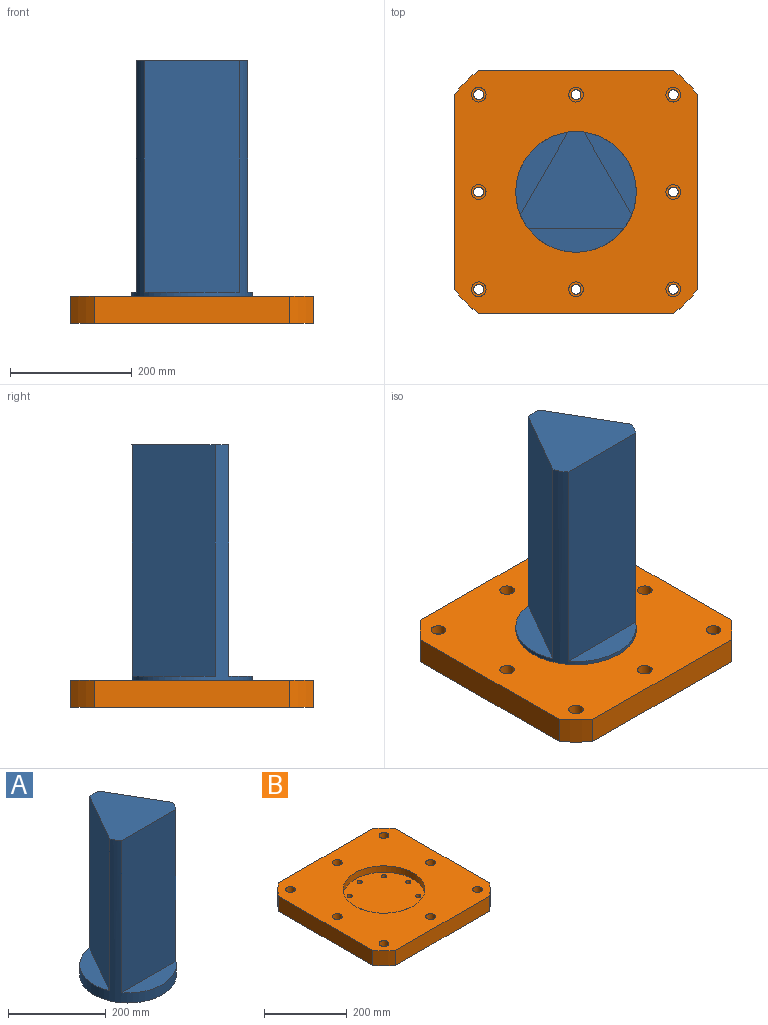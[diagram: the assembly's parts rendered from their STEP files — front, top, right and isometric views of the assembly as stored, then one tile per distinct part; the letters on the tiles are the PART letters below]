
ASSEMBLY  parts=2 mates=2
PART A: 27 faces, bbox 198.1x198.1x406.4 mm
  f0: plane 381x157.15mm, normal (0,-1,0), area 59872.9mm2, adj f3,f4,f5
  f1: plane 381x136.09mm, normal (0.87,0.5,0), area 59872.9mm2, adj f3,f4,f7
  f2: plane 381x136.09mm, normal (-0.87,0.5,0), area 59872.9mm2, adj f3,f4,f6
  f3: cylinder r=99.06mm len=406.4mm, axis (0,0,-1), area 45512.4mm2, adj f0,f1,f2,f4,f5,f6,f7,f8
  f4: plane 183.06x159.39mm, normal (0,0,1), area 18081.2mm2, adj f0,f1,f2,f3
  f5: plane 157.15x38.74mm, normal (0,0,1), area 4249mm2, adj f0,f3
  f6: plane 136.09x86.1mm, normal (0,0,1), area 4249mm2, adj f2,f3
  f7: plane 136.09x86.1mm, normal (0,0,1), area 4249mm2, adj f1,f3
  f8: plane 198.12x198.12mm, normal (0,0,-1), area 30016.4mm2, adj f3,f9,f11,f13,f15,f17,f19,f21
  f9: cylinder r=5.36mm len=19.05mm, axis (0,0,-1), area 641.3mm2, adj f8,f10
  f10: cone r=0mm half-angle=59deg, axis (0,0,-1), area 105.2mm2, adj f9
  f11: cylinder r=5.36mm len=19.05mm, axis (0,0,-1), area 641.3mm2, adj f8,f12
  f12: cone r=0mm half-angle=59deg, axis (0,0,-1), area 105.2mm2, adj f11
  f13: cylinder r=5.36mm len=19.05mm, axis (0,0,-1), area 641.3mm2, adj f8,f14
  f14: cone r=0mm half-angle=59deg, axis (0,0,-1), area 105.2mm2, adj f13
  f15: cylinder r=5.36mm len=19.05mm, axis (0,0,-1), area 641.3mm2, adj f8,f16
  f16: cone r=0mm half-angle=59deg, axis (0,0,-1), area 105.2mm2, adj f15
  f17: cylinder r=5.36mm len=19.05mm, axis (0,0,-1), area 641.3mm2, adj f8,f18
  f18: cone r=0mm half-angle=59deg, axis (0,0,-1), area 105.2mm2, adj f17
  f19: cylinder r=5.36mm len=19.05mm, axis (0,0,-1), area 641.3mm2, adj f8,f20
  f20: cone r=0mm half-angle=59deg, axis (0,0,-1), area 105.2mm2, adj f19
  f21: cylinder r=5.36mm len=19.05mm, axis (0,0,-1), area 641.3mm2, adj f8,f22
  f22: cone r=0mm half-angle=59deg, axis (0,0,-1), area 105.2mm2, adj f21
  f23: cylinder r=5.36mm len=19.05mm, axis (0,0,-1), area 641.3mm2, adj f8,f24
  f24: cone r=0mm half-angle=59deg, axis (0,0,-1), area 105.2mm2, adj f23
  f25: cylinder r=5.36mm len=19.05mm, axis (0,0,-1), area 641.3mm2, adj f8,f26
  f26: cone r=0mm half-angle=59deg, axis (0,0,-1), area 105.2mm2, adj f25
PART B: 62 faces, bbox 400.1x400.1x44.5 mm
  f0: plane 321.27x44.45mm, normal (1,0,0), area 14280.2mm2, adj f4,f5,f8,f9
  f1: plane 321.27x44.45mm, normal (0,1,0), area 14280.2mm2, adj f4,f5,f7,f8
  f2: plane 321.27x44.45mm, normal (-1,0,0), area 14280.2mm2, adj f4,f5,f6,f7
  f3: plane 321.27x44.45mm, normal (0,-1,0), area 14280.2mm2, adj f4,f5,f6,f9
  f4: plane 400.05x400.05mm, normal (0,0,-1), area 151199.6mm2, adj f0,f1,f2,f3,f6,f7,f8,f9
  f5: plane 400.05x400.05mm, normal (0,0,1), area 122675.4mm2, adj f0,f1,f2,f3,f6,f7,f8,f9
  f6: cylinder r=256.54mm len=44.45mm, axis (0,0,1), area 2481.2mm2, adj f2,f3,f4,f5
  f7: cylinder r=256.54mm len=44.45mm, axis (0,0,1), area 2481.2mm2, adj f1,f2,f4,f5
  f8: cylinder r=256.54mm len=44.45mm, axis (0,0,1), area 2481.2mm2, adj f0,f1,f4,f5
  f9: cylinder r=256.54mm len=44.45mm, axis (0,0,1), area 2481.2mm2, adj f0,f3,f4,f5
  f10: cylinder r=99.06mm len=198.12mm, axis (0,0,1), area 11857mm2, adj f5,f11
  f11: plane 198.12x198.12mm, normal (0,0,1), area 29753mm2, adj f10,f36,f39,f42,f45,f48,f51,f54
  f12: cylinder r=8.13mm len=27.94mm, axis (0,0,1), area 1426.9mm2, adj f4,f13
  f13: plane 24.13x24.13mm, normal (0,0,1), area 249.8mm2, adj f12,f14
  f14: cylinder r=12.06mm len=24.13mm, axis (0,0,1), area 1251.6mm2, adj f5,f13
  f15: cylinder r=8.13mm len=27.94mm, axis (0,0,1), area 1426.9mm2, adj f4,f16
  f16: plane 24.13x24.13mm, normal (0,0,1), area 249.8mm2, adj f15,f17
  f17: cylinder r=12.06mm len=24.13mm, axis (0,0,1), area 1251.6mm2, adj f5,f16
  f18: cylinder r=8.13mm len=27.94mm, axis (0,0,1), area 1426.9mm2, adj f4,f19
  f19: plane 24.13x24.13mm, normal (0,0,1), area 249.8mm2, adj f18,f20
  f20: cylinder r=12.06mm len=24.13mm, axis (0,0,1), area 1251.6mm2, adj f5,f19
  f21: cylinder r=8.13mm len=27.94mm, axis (0,0,1), area 1426.9mm2, adj f4,f22
  f22: plane 24.13x24.13mm, normal (0,0,1), area 249.8mm2, adj f21,f23
  f23: cylinder r=12.06mm len=24.13mm, axis (0,0,1), area 1251.6mm2, adj f5,f22
  f24: cylinder r=8.13mm len=27.94mm, axis (0,0,1), area 1426.9mm2, adj f4,f25
  f25: plane 24.13x24.13mm, normal (0,0,1), area 249.8mm2, adj f24,f26
  f26: cylinder r=12.06mm len=24.13mm, axis (0,0,1), area 1251.6mm2, adj f5,f25
  f27: cylinder r=8.13mm len=27.94mm, axis (0,0,1), area 1426.9mm2, adj f4,f28
  f28: plane 24.13x24.13mm, normal (0,0,1), area 249.8mm2, adj f27,f29
  f29: cylinder r=12.06mm len=24.13mm, axis (0,0,1), area 1251.6mm2, adj f5,f28
  f30: cylinder r=8.13mm len=27.94mm, axis (0,0,1), area 1426.9mm2, adj f4,f31
  f31: plane 24.13x24.13mm, normal (0,0,1), area 249.8mm2, adj f30,f32
  f32: cylinder r=12.06mm len=24.13mm, axis (0,0,1), area 1251.6mm2, adj f5,f31
  f33: cylinder r=8.13mm len=27.94mm, axis (0,0,1), area 1426.9mm2, adj f4,f34
  f34: plane 24.13x24.13mm, normal (0,0,1), area 249.8mm2, adj f33,f35
  f35: cylinder r=12.06mm len=24.13mm, axis (0,0,1), area 1251.6mm2, adj f5,f34
  f36: cylinder r=6.54mm len=13.08mm, axis (0,0,-1), area 495.8mm2, adj f11,f37
  f37: plane 19.3x19.3mm, normal (0,0,-1), area 158.3mm2, adj f36,f38
  f38: cylinder r=9.65mm len=19.3mm, axis (0,0,-1), area 808.7mm2, adj f4,f37
  f39: cylinder r=6.54mm len=13.08mm, axis (0,0,-1), area 495.8mm2, adj f11,f40
  f40: plane 19.3x19.3mm, normal (0,0,-1), area 158.3mm2, adj f39,f41
  f41: cylinder r=9.65mm len=19.3mm, axis (0,0,-1), area 808.7mm2, adj f4,f40
  f42: cylinder r=6.54mm len=13.08mm, axis (0,0,-1), area 495.8mm2, adj f11,f43
  f43: plane 19.3x19.3mm, normal (0,0,-1), area 158.3mm2, adj f42,f44
  f44: cylinder r=9.65mm len=19.3mm, axis (0,0,-1), area 808.7mm2, adj f4,f43
  f45: cylinder r=6.54mm len=13.08mm, axis (0,0,-1), area 495.8mm2, adj f11,f46
  f46: plane 19.3x19.3mm, normal (0,0,-1), area 158.3mm2, adj f45,f47
  f47: cylinder r=9.65mm len=19.3mm, axis (0,0,-1), area 808.7mm2, adj f4,f46
  f48: cylinder r=6.54mm len=13.08mm, axis (0,0,-1), area 495.8mm2, adj f11,f49
  f49: plane 19.3x19.3mm, normal (0,0,-1), area 158.3mm2, adj f48,f50
  f50: cylinder r=9.65mm len=19.3mm, axis (0,0,-1), area 808.7mm2, adj f4,f49
  f51: cylinder r=6.54mm len=13.08mm, axis (0,0,-1), area 495.8mm2, adj f11,f52
  f52: plane 19.3x19.3mm, normal (0,0,-1), area 158.3mm2, adj f51,f53
  f53: cylinder r=9.65mm len=19.3mm, axis (0,0,-1), area 808.7mm2, adj f4,f52
  f54: cylinder r=6.54mm len=13.08mm, axis (0,0,-1), area 495.8mm2, adj f11,f55
  f55: plane 19.3x19.3mm, normal (0,0,-1), area 158.3mm2, adj f54,f56
  f56: cylinder r=9.65mm len=19.3mm, axis (0,0,-1), area 808.7mm2, adj f4,f55
  f57: cylinder r=6.54mm len=13.08mm, axis (0,0,-1), area 495.8mm2, adj f11,f58
  f58: plane 19.3x19.3mm, normal (0,0,-1), area 158.3mm2, adj f57,f59
  f59: cylinder r=9.65mm len=19.3mm, axis (0,0,-1), area 808.7mm2, adj f4,f58
  f60: cylinder r=24.98mm len=49.96mm, axis (0,0,-1), area 2491.7mm2, adj f4,f61
  f61: plane 49.96x49.96mm, normal (0,0,-1), area 1960.5mm2, adj f60
PLACE A t=(-197.25,129.01,95.35)mm
PLACE B t=(-197.25,129.01,89)mm
MATE cylindrical A.f3 <-> B.f10  axis (0,0,-1) through (-197.25,129.01,69.95)mm
MATE planar A.f3 <-> B.f10  axis (0,0,-1) through (-197.25,129.01,69.95)mm
